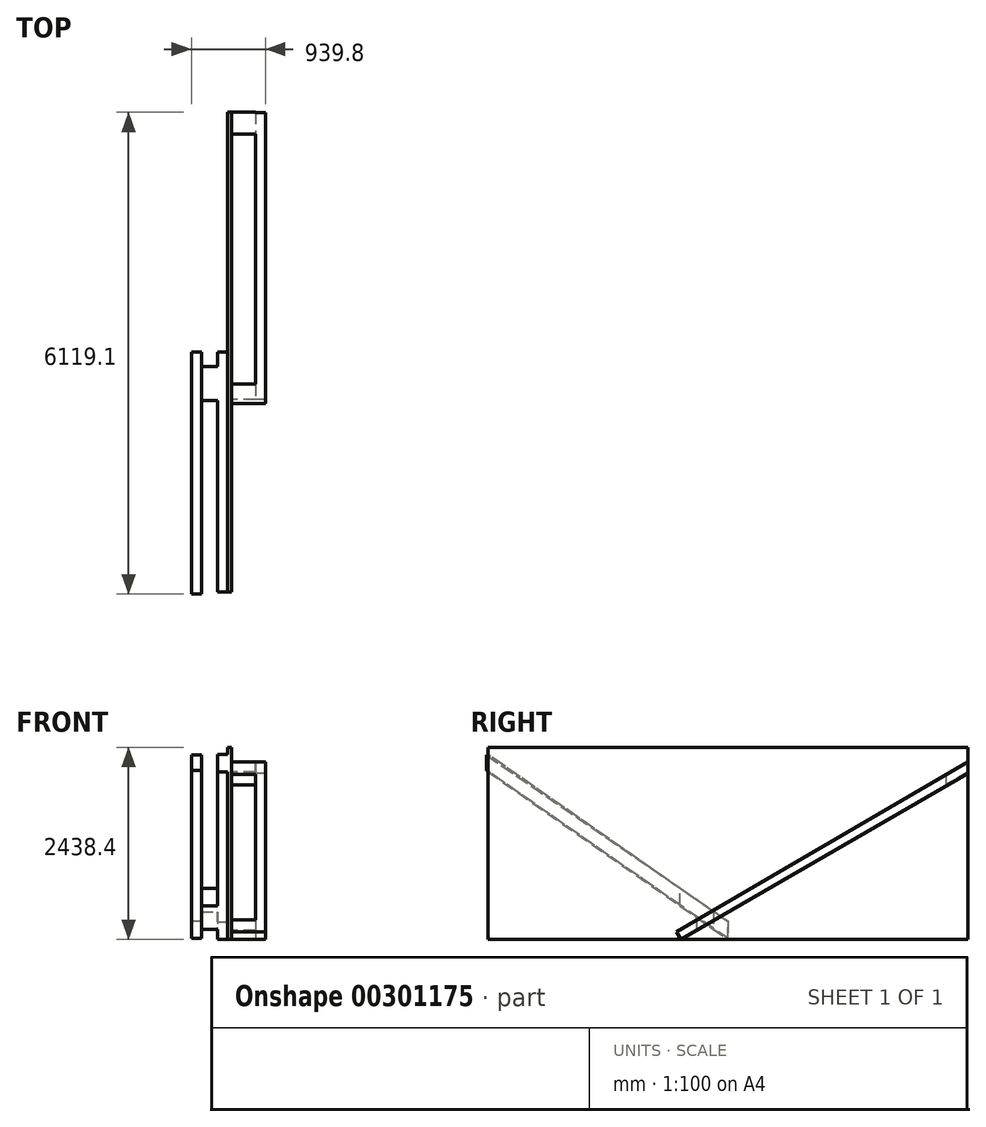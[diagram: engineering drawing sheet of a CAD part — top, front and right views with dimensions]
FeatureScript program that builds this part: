
annotation { "Feature Type Name" : "Feature", "Feature Type Description" : "" }
export const myFeature = defineFeature(function(context is Context, id is Id, definition is map)
    precondition{}
    {
        {
            var Q0;
            Q0=qCreatedBy(makeId("Right.planeOp"),FACE);
            var sketch = newSketch(context, id + "F0", { "sketchPlane" : qUnion([Q0])});
            skLineSegment(sketch, "E0.bottom", {"start": v(-3048, -1219.2) * mm, "end": v(3048, -1219.2) * mm});
            skLineSegment(sketch, "E0.top", {"start": v(-3048, 1219.2) * mm, "end": v(3048, 1219.2) * mm});
            skLineSegment(sketch, "E0.left", {"start": v(-3048, -1219.2) * mm, "end": v(-3048, 1219.2) * mm});
            skLineSegment(sketch, "E0.right", {"start": v(3048, -1219.2) * mm, "end": v(3048, 1219.2) * mm});
            skPoint(sketch, "E0.middle", {"position": v(0, 0) * mm});
            skSolve(sketch);
        }
        {
            var Q0;
            Q0 = qSketchRegion(id + "F0", true);
            extrude(context, id + "F1", {"entities" : qUnion([Q0]), "depth" : 50.8 * mm});
        }
        {
            var Q0;
            Q0=makeQuery(id+"F1.opExtrude","CAP_FACE",FACE,{"disambiguationData":[OSD([sQuery(id+"F0.wireOp",EDGE,"E0.bottom"),sQuery(id+"F0.wireOp",EDGE,"E0.top"),sQuery(id+"F0.wireOp",EDGE,"E0.left"),sQuery(id+"F0.wireOp",EDGE,"E0.right")])],"isStart":false});
            var sketch = newSketch(context, id + "F2", { "sketchPlane" : qUnion([Q0])});
            skLineSegment(sketch, "E1", {"start": v(3048, 905.65) * mm, "end": v(2768.72, 742.92) * mm});
            skPoint(sketch, "E2", {"position": v(1224.66, -156.77) * mm});
            skLineSegment(sketch, "E3", {"start": v(-598.68, -1219.2) * mm, "end": v(-655.6, -1121.51) * mm});
            skLineSegment(sketch, "E4", {"start": v(-655.6, -1121.51) * mm, "end": v(-403.77, -974.77) * mm});
            skLineSegment(sketch, "E5", {"start": v(3048, 905.65) * mm, "end": v(3048, 1036.5) * mm});
            skLineSegment(sketch, "E6", {"start": v(-403.77, -974.77) * mm, "end": v(-403.77, -1105.63) * mm});
            skLineSegment(sketch, "E7", {"start": v(2768.72, 873.78) * mm, "end": v(2768.72, 742.92) * mm});
            skLineSegment(sketch, "E8.trimOffspring", {"start": v(2768.72, 873.78) * mm, "end": v(3048, 1036.5) * mm});
            skLineSegment(sketch, "E9.trimOffspring", {"start": v(-403.77, -1105.63) * mm, "end": v(-598.68, -1219.2) * mm});
            skSolve(sketch);
        }
        {
            var Q0;
            Q0 = qSketchRegion(id + "F2", true);
            extrude(context, id + "F3", {"entities" : qUnion([Q0]), "operationType" : NewBodyOperationType.ADD, "depth" : 304.8 * mm});
        }
        {
            var Q0;
            Q0=makeQuery(id+"F1.opExtrude","CAP_FACE",FACE,{"disambiguationData":[OSD([sQuery(id+"F0.wireOp",EDGE,"E0.bottom"),sQuery(id+"F0.wireOp",EDGE,"E0.top"),sQuery(id+"F0.wireOp",EDGE,"E0.left"),sQuery(id+"F0.wireOp",EDGE,"E0.right")])],"isStart":true});
            var sketch = newSketch(context, id + "F4", { "sketchPlane" : qUnion([Q0])});
            skLineSegment(sketch, "E10", {"start": v(3048, 908.16) * mm, "end": v(0, -1219.2) * mm});
            skLineSegment(sketch, "E11", {"start": v(0, -1219.2) * mm, "end": v(0, -999.25) * mm});
            skLineSegment(sketch, "E12", {"start": v(0, -999.25) * mm, "end": v(3048, 1128.1) * mm});
            skLineSegment(sketch, "E13", {"start": v(3048, 1128.1) * mm, "end": v(3048, 908.16) * mm});
            skSolve(sketch);
        }
        {
            var Q0;
            Q0=makeQuery(id+"F4.imprint","IMPRINT",FACE,{"disambiguationData":[TD([[makeQuery(id+"F4.imprint","IMPRINT",EDGE,{"derivedFrom":sQuery(id+"F4.wireOp",EDGE,"E10")}),-1.0]])]});
            extrude(context, id + "F5", {"entities" : qUnion([Q0]), "operationType" : NewBodyOperationType.ADD, "depth" : 127 * mm});
        }
        {
            var Q0;
            Q0=makeQuery(id+"F5.opExtrude","CAP_FACE",FACE,{"disambiguationData":[OSD([sQuery(id+"F4.wireOp",EDGE,"E10"),sQuery(id+"F4.wireOp",EDGE,"E11"),sQuery(id+"F4.wireOp",EDGE,"E12"),sQuery(id+"F4.wireOp",EDGE,"E13")])],"isStart":false});
            var sketch = newSketch(context, id + "F6", { "sketchPlane" : qUnion([Q0])});
            skLineSegment(sketch, "E14", {"start": v(184.84, -870.25) * mm, "end": v(184.84, -1090.2) * mm});
            skLineSegment(sketch, "E15", {"start": v(184.84, -1090.2) * mm, "end": v(611.34, -792.51) * mm});
            skLineSegment(sketch, "E16", {"start": v(611.34, -792.51) * mm, "end": v(611.34, -572.56) * mm});
            skLineSegment(sketch, "E17", {"start": v(611.34, -572.56) * mm, "end": v(184.84, -870.25) * mm});
            skSolve(sketch);
        }
        {
            var Q0;
            Q0=makeQuery(id+"F6.imprint","IMPRINT",FACE,{"disambiguationData":[TD([[makeQuery(id+"F6.imprint","IMPRINT",EDGE,{"derivedFrom":sQuery(id+"F6.wireOp",EDGE,"E14")}),1.0]])]});
            extrude(context, id + "F7", {"entities" : qUnion([Q0]), "operationType" : NewBodyOperationType.ADD, "depth" : 203.2 * mm});
        }
        {
            var Q0;
            Q0=makeQuery(id+"F7.opExtrude","CAP_FACE",FACE,{"disambiguationData":[OSD([sQuery(id+"F6.wireOp",EDGE,"E14"),sQuery(id+"F6.wireOp",EDGE,"E15"),sQuery(id+"F6.wireOp",EDGE,"E16"),sQuery(id+"F6.wireOp",EDGE,"E17")])],"isStart":false});
            var sketch = newSketch(context, id + "F8", { "sketchPlane" : qUnion([Q0])});
            skSolve(sketch);
        }
        {
            var Q0;
            Q0=makeQuery(id+"F8.imprint","IMPRINT",FACE,{"disambiguationData":[TD([[makeQuery(id+"F8.imprint","IMPRINT",EDGE,{"derivedFrom":makeQuery(id+"F7.opExtrude","CAP_EDGE",EDGE,{"disambiguationData":[OSD([sQuery(id+"F6.wireOp",EDGE,"E14")])],"isStart":false})}),1.0]])]});
            var sketch = newSketch(context, id + "F9", { "sketchPlane" : qUnion([Q0])});
            skLineSegment(sketch, "E18", {"start": v(0, -1209.7) * mm, "end": v(3071.1, 929.14) * mm});
            skLineSegment(sketch, "E19", {"start": v(3071.1, 929.14) * mm, "end": v(3071.1, 1121.74) * mm});
            skLineSegment(sketch, "E20", {"start": v(3071.1, 1121.74) * mm, "end": v(0, -986.7) * mm});
            skLineSegment(sketch, "E21", {"start": v(0, -986.7) * mm, "end": v(0, -1209.7) * mm});
            skLineSegment(sketch, "E22", {"start": v(0, -1209.7) * mm, "end": v(0, -986.7) * mm});
            skSolve(sketch);
        }
        {
            var Q0;
            {var subQ5=makeQuery(id+"F8.imprint","IMPRINT",EDGE,{"derivedFrom":makeQuery(id+"F7.opExtrude","CAP_EDGE",EDGE,{"disambiguationData":[OSD([sQuery(id+"F6.wireOp",EDGE,"E17")])],"isStart":false})});Q0=makeQuery(id+"F9.imprint","IMPRINT",FACE,{"disambiguationData":[TD([[makeQuery(id+"F9.imprint","IMPRINT",EDGE,{"derivedFrom":subQ5}),-1.0]])]});}
            var Q1;
            {var subQ0=sQuery(id+"F9.wireOp",EDGE,"E19");Q1=makeQuery(id+"F9.imprint","IMPRINT",FACE,{"disambiguationData":[TD([[makeQuery(id+"F9.imprint","IMPRINT",EDGE,{"derivedFrom":subQ0}),1.0]])]});}
            extrude(context, id + "F10", {"entities" : qUnion([Q0, Q1]), "operationType" : NewBodyOperationType.ADD, "depth" : 127 * mm});
        }
        {
            var Q0;
            Q0=makeQuery(id+"F3.opExtrude","CAP_FACE",FACE,{"disambiguationData":[OSD([sQuery(id+"F2.wireOp",EDGE,"E3"),sQuery(id+"F2.wireOp",EDGE,"E4"),sQuery(id+"F2.wireOp",EDGE,"E6"),sQuery(id+"F2.wireOp",EDGE,"E9.trimOffspring")])],"isStart":false});
            var sketch = newSketch(context, id + "F11", { "sketchPlane" : qUnion([Q0])});
            skLineSegment(sketch, "E23", {"start": v(-655.6, -1121.51) * mm, "end": v(3045.2, 1034.87) * mm});
            skLineSegment(sketch, "E24", {"start": v(3045.2, 1034.87) * mm, "end": v(3045.2, 886.5) * mm});
            skLineSegment(sketch, "E25", {"start": v(3045.2, 886.5) * mm, "end": v(-598.68, -1219.2) * mm});
            skLineSegment(sketch, "E26", {"start": v(-598.68, -1219.2) * mm, "end": v(-655.6, -1121.51) * mm});
            skSolve(sketch);
        }
        {
            var Q0;
            Q0 = qSketchRegion(id + "F11", true);
            extrude(context, id + "F12", {"entities" : qUnion([Q0]), "operationType" : NewBodyOperationType.ADD, "depth" : 127 * mm});
        }
    });
